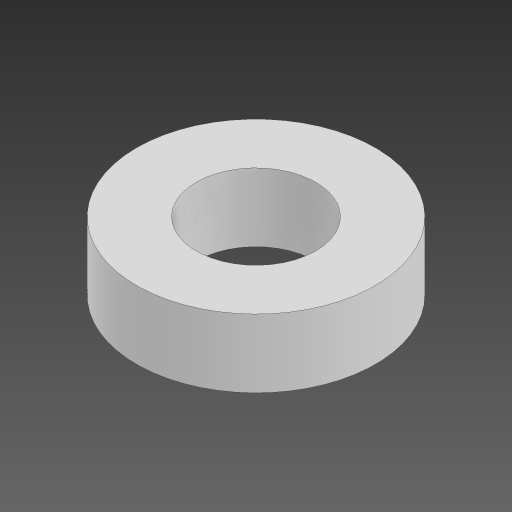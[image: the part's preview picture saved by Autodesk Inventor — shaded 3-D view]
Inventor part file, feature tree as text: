
AUTODESK INVENTOR PART (.ipt)
format: ipt  version: 2024 (Build 280153000, 153)  size: 92,160 bytes
history: native  units: mm
features: extrude x1, sketch x1
ambient origin geometry x8: Origin, YZ Plane, XZ Plane, XY Plane, X Axis, Y Axis, Z Axis, Center Point
bodies: Solid1 (feature_tree)
feature tree (2):
  extrude  "Extrusion1"  Depth=3.5mm
  sketch  "Sketch1"  dims[d0=7.0mm d1=3.5mm d2=2.0mm d3=0.0mm]
